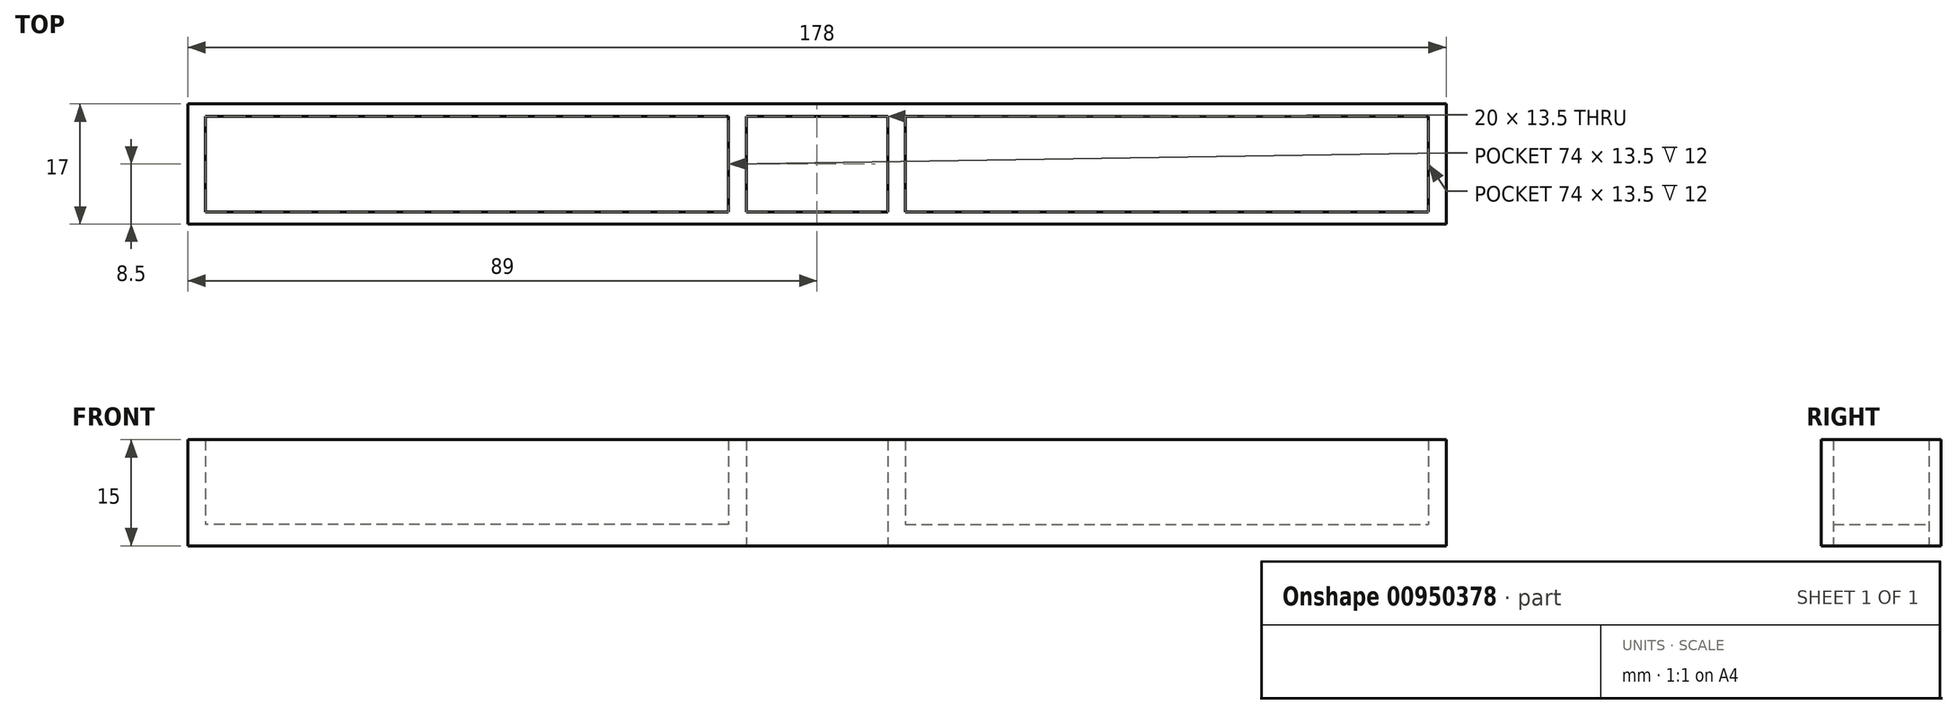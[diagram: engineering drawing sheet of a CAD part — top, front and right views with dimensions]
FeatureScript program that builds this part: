
annotation { "Feature Type Name" : "Feature", "Feature Type Description" : "" }
export const myFeature = defineFeature(function(context is Context, id is Id, definition is map)
    precondition{}
    {
        {
            var Q0;
            Q0=qCreatedBy(makeId("Top.planeOp"),FACE);
            var sketch = newSketch(context, id + "F0", { "sketchPlane" : qUnion([Q0])});
            skLineSegment(sketch, "E0.bottom", {"start": v(-89, -8.5) * mm, "end": v(89, -8.5) * mm});
            skLineSegment(sketch, "E0.top", {"start": v(-89, 8.5) * mm, "end": v(89, 8.5) * mm});
            skLineSegment(sketch, "E0.left", {"start": v(-89, -8.5) * mm, "end": v(-89, 8.5) * mm});
            skLineSegment(sketch, "E0.right", {"start": v(89, -8.5) * mm, "end": v(89, 8.5) * mm});
            skPoint(sketch, "E0.middle", {"position": v(0, 0) * mm});
            skLineSegment(sketch, "E1.bottom", {"start": v(-12.5, -6.75) * mm, "end": v(12.5, -6.75) * mm});
            skLineSegment(sketch, "E1.top", {"start": v(-12.5, 6.75) * mm, "end": v(12.5, 6.75) * mm});
            skLineSegment(sketch, "E1.left", {"start": v(-12.5, -6.75) * mm, "end": v(-12.5, 6.75) * mm});
            skLineSegment(sketch, "E1.right", {"start": v(12.5, -6.75) * mm, "end": v(12.5, 6.75) * mm});
            skLineSegment(sketch, "E2", {"start": v(12.5, 6.75) * mm, "end": v(86.5, 6.75) * mm});
            skLineSegment(sketch, "E3", {"start": v(12.5, -6.75) * mm, "end": v(86.5, -6.75) * mm});
            skLineSegment(sketch, "E4", {"start": v(86.5, -6.75) * mm, "end": v(86.5, 6.75) * mm});
            skLineSegment(sketch, "E5", {"start": v(-12.5, 6.75) * mm, "end": v(-86.5, 6.75) * mm});
            skLineSegment(sketch, "E6", {"start": v(-12.5, -6.75) * mm, "end": v(-86.5, -6.75) * mm});
            skLineSegment(sketch, "E7", {"start": v(-86.5, -6.75) * mm, "end": v(-86.5, 6.75) * mm});
            skLineSegment(sketch, "E8", {"start": v(-10, 6.75) * mm, "end": v(-10, -6.75) * mm});
            skLineSegment(sketch, "E9", {"start": v(10, 6.75) * mm, "end": v(10, -6.75) * mm});
            skSolve(sketch);
        }
        {
            var Q0;
            Q0=makeQuery(id+"F0.imprint","IMPRINT",FACE,{"disambiguationData":[TD([[makeQuery(id+"F0.imprint","IMPRINT",EDGE,{"derivedFrom":sQuery(id+"F0.wireOp",EDGE,"E0.bottom")}),1.0]])]});
            var Q1;
            {var subQ0=sQuery(id+"F0.wireOp",EDGE,"E1.left");Q1=makeQuery(id+"F0.imprint","IMPRINT",FACE,{"disambiguationData":[TD([[makeQuery(id+"F0.imprint","IMPRINT",EDGE,{"derivedFrom":subQ0}),-1.0]])]});}
            var Q2;
            {var subQ0=sQuery(id+"F0.wireOp",EDGE,"E1.right");Q2=makeQuery(id+"F0.imprint","IMPRINT",FACE,{"disambiguationData":[TD([[makeQuery(id+"F0.imprint","IMPRINT",EDGE,{"derivedFrom":subQ0}),1.0]])]});}
            extrude(context, id + "F1", {"entities" : qUnion([Q0, Q1, Q2]), "depth" : 15 * mm, "offsetDistance" : 25 * mm});
        }
        {
            var Q0;
            Q0=makeQuery(id+"F0.imprint","IMPRINT",FACE,{"disambiguationData":[TD([[makeQuery(id+"F0.imprint","IMPRINT",EDGE,{"derivedFrom":sQuery(id+"F0.wireOp",EDGE,"E1.left")}),1.0]])]});
            var Q1;
            Q1=makeQuery(id+"F0.imprint","IMPRINT",FACE,{"disambiguationData":[TD([[makeQuery(id+"F0.imprint","IMPRINT",EDGE,{"derivedFrom":sQuery(id+"F0.wireOp",EDGE,"E1.right")}),-1.0]])]});
            extrude(context, id + "F2", {"entities" : qUnion([Q0, Q1]), "operationType" : NewBodyOperationType.ADD, "depth" : 3 * mm, "offsetDistance" : 25 * mm});
        }
    });
